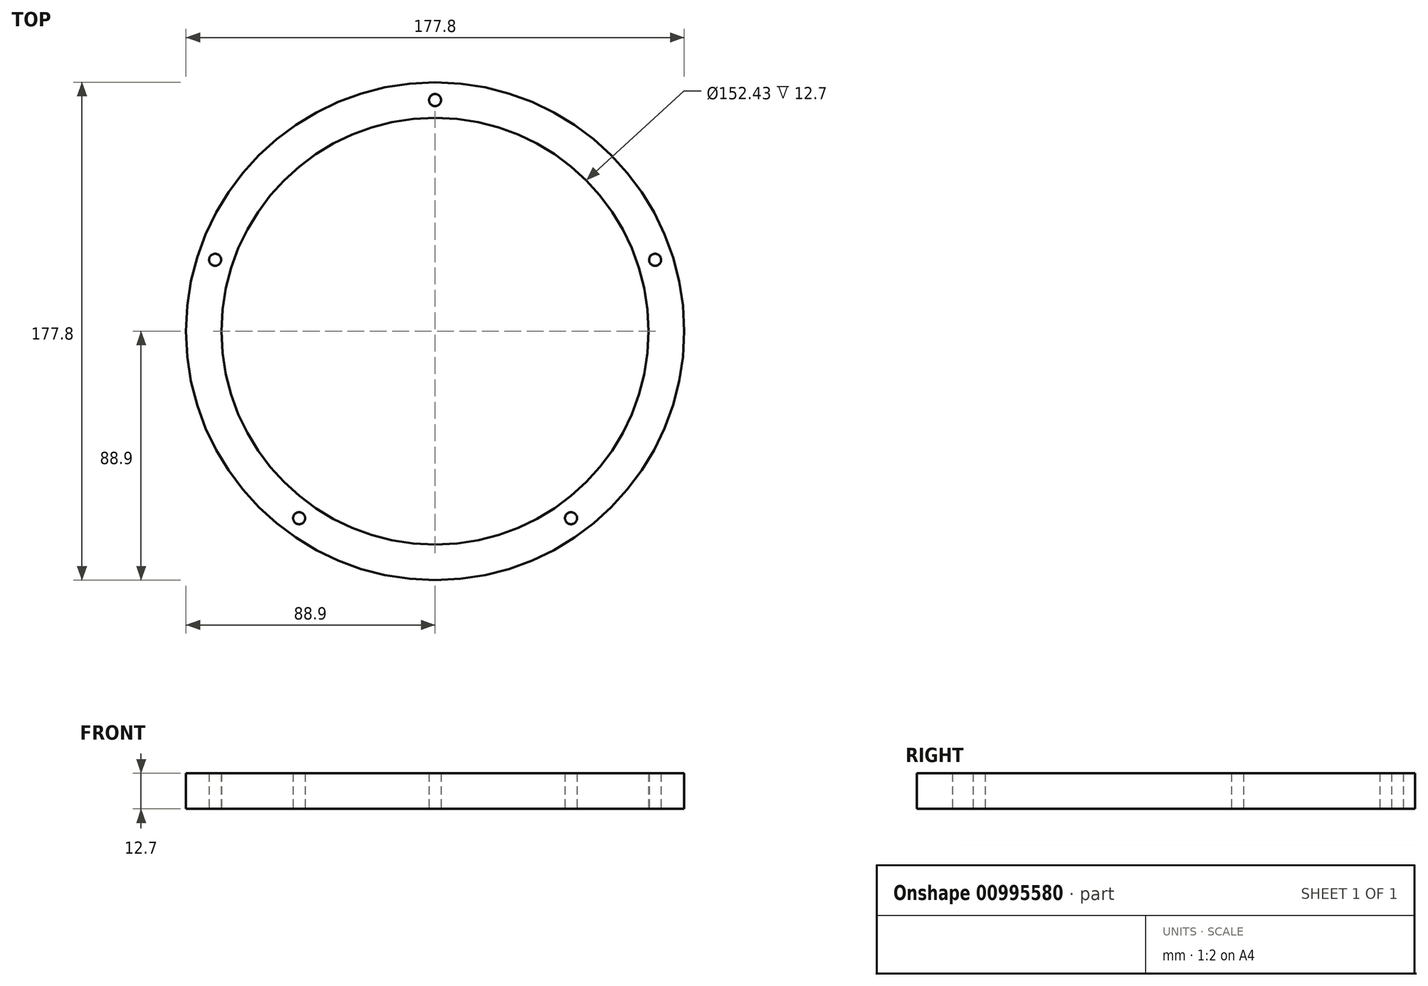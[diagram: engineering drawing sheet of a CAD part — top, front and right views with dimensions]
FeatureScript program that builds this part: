
annotation { "Feature Type Name" : "Feature", "Feature Type Description" : "" }
export const myFeature = defineFeature(function(context is Context, id is Id, definition is map)
    precondition{}
    {
        {
            var Q0;
            Q0=qCreatedBy(makeId("Top.planeOp"),FACE);
            var sketch = newSketch(context, id + "F0", { "sketchPlane" : qUnion([Q0])});
            skCircle(sketch, "E0", {"center": v(0, 0) * mm, "radius": 76.21 * mm});
            skCircle(sketch, "E1", {"center": v(0, 0) * mm, "radius": 88.9 * mm});
            skCircle(sketch, "E2", {"center": v(0, 0) * mm, "radius": 82.55 * mm, "construction": true});
            skCircle(sketch, "E3", {"center": v(0, 82.55) * mm, "radius": 2.15 * mm});
            skCircle(sketch, "E4.1.0", {"center": v(-78.5, 25.5) * mm, "radius": 2.15 * mm});
            skCircle(sketch, "E4.2.0", {"center": v(-48.52, -66.78) * mm, "radius": 2.15 * mm});
            skCircle(sketch, "E4.3.0", {"center": v(48.52, -66.78) * mm, "radius": 2.15 * mm});
            skCircle(sketch, "E4.4.0", {"center": v(78.5, 25.5) * mm, "radius": 2.15 * mm});
            skSolve(sketch);
        }
        {
            var Q0;
            Q0=makeQuery(id+"F0.imprint","IMPRINT",FACE,{"disambiguationData":[TD([[makeQuery(id+"F0.imprint","IMPRINT",EDGE,{"derivedFrom":sQuery(id+"F0.wireOp",EDGE,"E0")}),-1.0]])]});
            extrude(context, id + "F1", {"entities" : qUnion([Q0]), "depth" : 12.7 * mm, "offsetDistance" : 25.4 * mm});
        }
        {
            var Q0;
            Q0=makeQuery(id+"F0.imprint","IMPRINT",FACE,{"disambiguationData":[TD([[makeQuery(id+"F0.imprint","IMPRINT",EDGE,{"derivedFrom":sQuery(id+"F0.wireOp",EDGE,"E4.1.0")}),-1.0]])]});
            var Q1;
            Q1=makeQuery(id+"F0.imprint","IMPRINT",FACE,{"disambiguationData":[TD([[makeQuery(id+"F0.imprint","IMPRINT",EDGE,{"derivedFrom":sQuery(id+"F0.wireOp",EDGE,"E3")}),-1.0]])]});
            var Q2;
            Q2=makeQuery(id+"F0.imprint","IMPRINT",FACE,{"disambiguationData":[TD([[makeQuery(id+"F0.imprint","IMPRINT",EDGE,{"derivedFrom":sQuery(id+"F0.wireOp",EDGE,"E4.4.0")}),-1.0]])]});
            var Q3;
            Q3=makeQuery(id+"F0.imprint","IMPRINT",FACE,{"disambiguationData":[TD([[makeQuery(id+"F0.imprint","IMPRINT",EDGE,{"derivedFrom":sQuery(id+"F0.wireOp",EDGE,"E4.3.0")}),-1.0]])]});
            var Q4;
            Q4=makeQuery(id+"F0.imprint","IMPRINT",FACE,{"disambiguationData":[TD([[makeQuery(id+"F0.imprint","IMPRINT",EDGE,{"derivedFrom":sQuery(id+"F0.wireOp",EDGE,"E4.2.0")}),-1.0]])]});
            extrude(context, id + "F2", {"entities" : qUnion([Q0, Q1, Q2, Q3, Q4]), "operationType" : NewBodyOperationType.ADD, "depth" : 6.35 * mm, "offsetDistance" : 25.4 * mm});
        }
    });
